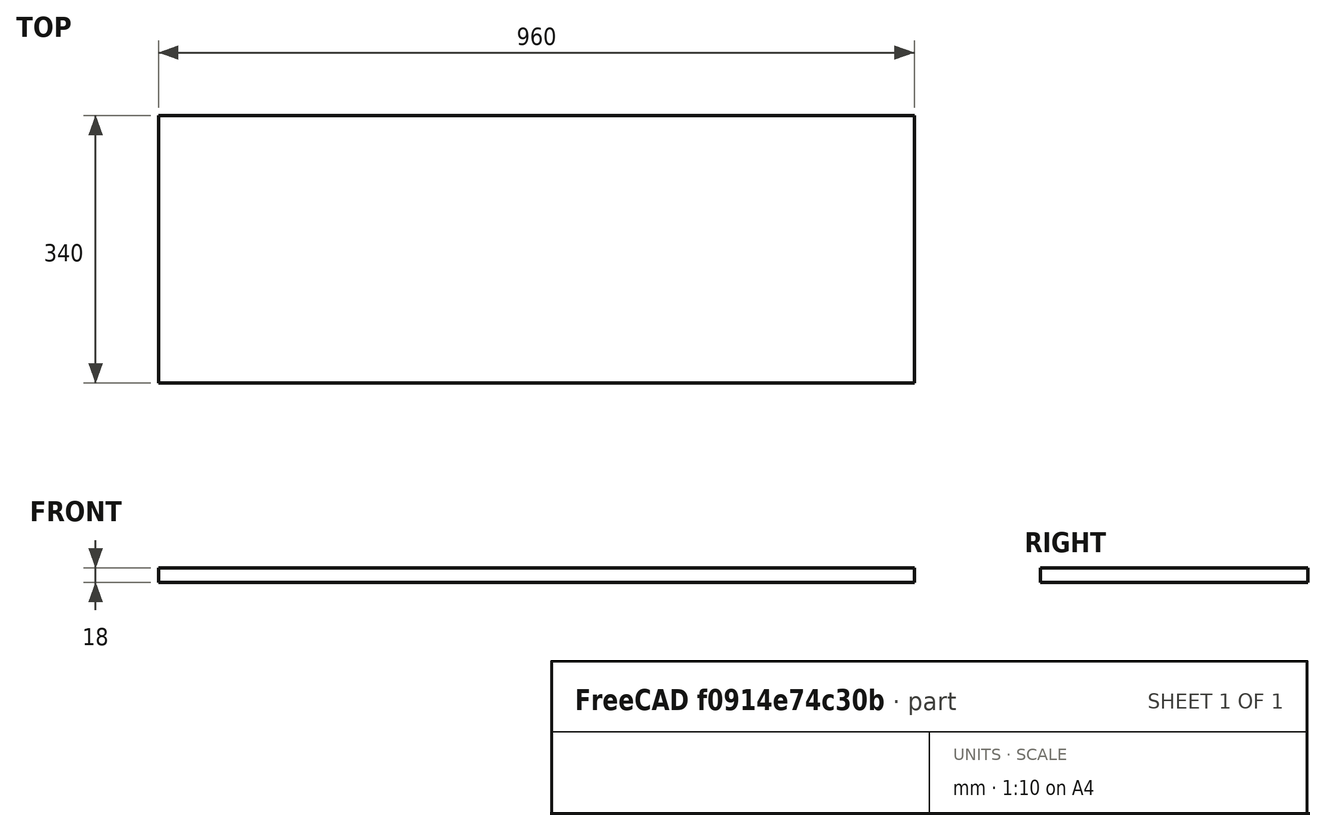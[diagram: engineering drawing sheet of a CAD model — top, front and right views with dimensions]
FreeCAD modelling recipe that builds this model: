
FCSTD DOCUMENT  (FreeCAD 0.19R24366 (Git))
Label: table
License: All rights reserved
LicenseURL: http://en.wikipedia.org/wiki/All_rights_reserved
objects: Sketcher::SketchObject×1, Part::Extrusion×1
note: 2 computed .brp shape members not serialized (recipe doc carries the construction recipe); baked Part::Feature solids carry a one-line shape summary decoded from their .brp

FEATURE [Sketcher::SketchObject] Sketch
  FullyConstrained = true
  sketch-geometry (4):
    g0: LineSegment StartX=-480 StartY=170 StartZ=0 EndX=480 EndY=170 EndZ=0
    g1: LineSegment StartX=480 StartY=170 StartZ=0 EndX=480 EndY=-170 EndZ=0
    g2: LineSegment StartX=480 StartY=-170 StartZ=0 EndX=-480 EndY=-170 EndZ=0
    g3: LineSegment StartX=-480 StartY=-170 StartZ=0 EndX=-480 EndY=170 EndZ=0
  constraints (11):
    c: Coincident(g0,g1)
    c: Coincident(g1,g2)
    c: Coincident(g2,g3)
    c: Coincident(g3,g0)
    c: Horizontal(g0)
    c: Horizontal(g2)
    c: Vertical(g1)
    c: Vertical(g3)
    c: DistanceX(g0,g0) = 960
    c: DistanceY(g3,g3) = 340
    c: Symmetric(g0,g2,g-1)
FEATURE [Part::Extrusion] Extrude
  Base = -> Sketch
  Dir = (0,0,1)
  DirMode = 2
  FaceMakerClass = Part::FaceMakerBullseye
  LengthFwd = 18
  LengthRev = 0
  Solid = true
  Symmetric = false
